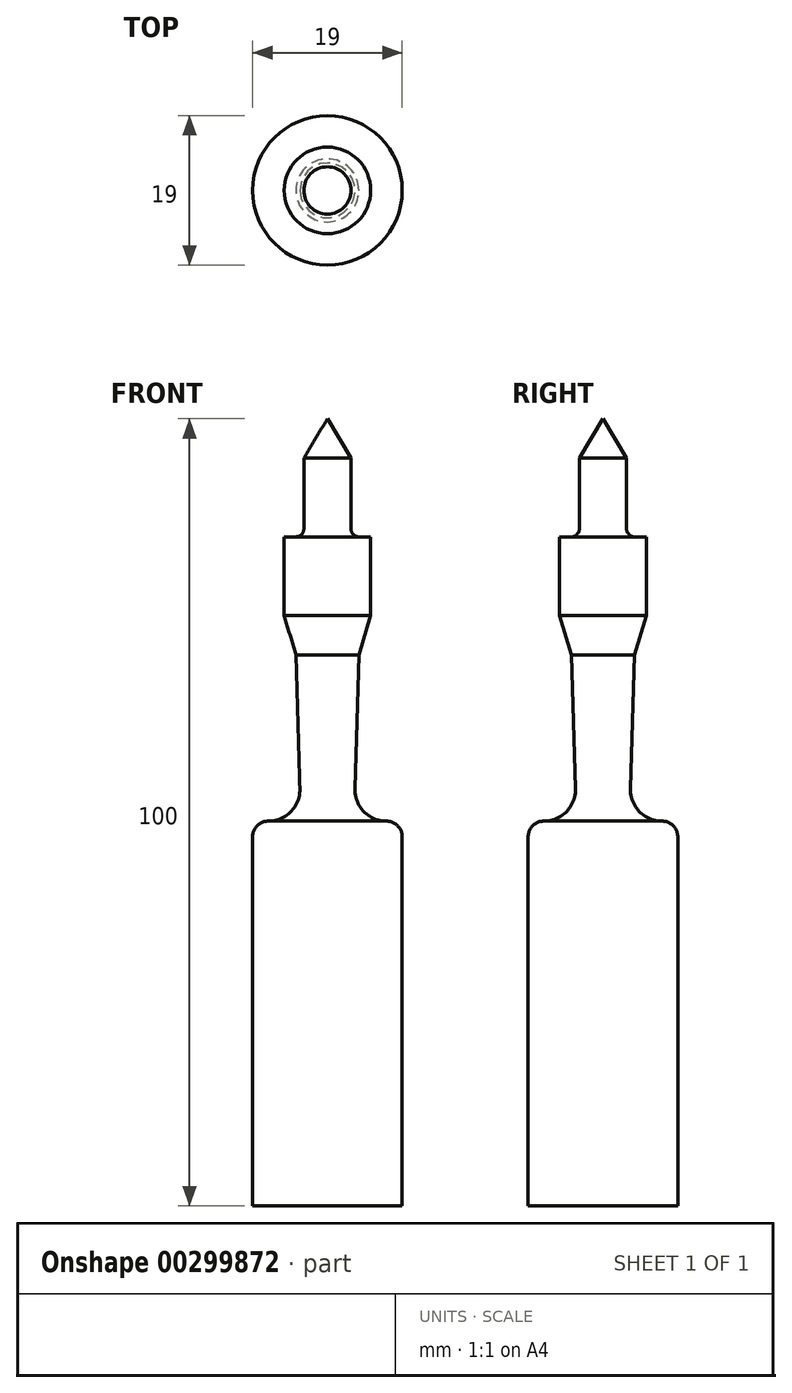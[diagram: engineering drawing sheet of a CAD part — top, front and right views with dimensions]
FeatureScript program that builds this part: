
annotation { "Feature Type Name" : "Feature", "Feature Type Description" : "" }
export const myFeature = defineFeature(function(context is Context, id is Id, definition is map)
    precondition{}
    {
        {
            var Q0;
            Q0=qCreatedBy(makeId("Front.planeOp"),FACE);
            var sketch = newSketch(context, id + "F0", { "sketchPlane" : qUnion([Q0])});
            skLineSegment(sketch, "E0", {"start": v(0, 0) * mm, "end": v(3, -5) * mm});
            skLineSegment(sketch, "E1", {"start": v(3, -5) * mm, "end": v(3, -14) * mm});
            skLineSegment(sketch, "E2", {"start": v(0, 0) * mm, "end": v(0, -100) * mm});
            skArc(sketch, "E3", {"start": v(3, -14) * mm, "mid": v(3.3, -14.7) * mm, "end": v(4, -15) * mm});
            skLineSegment(sketch, "E4", {"start": v(4, -15) * mm, "end": v(5.5, -15) * mm});
            skLineSegment(sketch, "E5", {"start": v(5.5, -15) * mm, "end": v(5.5, -25) * mm});
            skLineSegment(sketch, "E6", {"start": v(5.5, -25) * mm, "end": v(4, -30) * mm});
            skLineSegment(sketch, "E7", {"start": v(9.5, -53.12) * mm, "end": v(9.5, -100) * mm});
            skLineSegment(sketch, "E8", {"start": v(0, -100) * mm, "end": v(9.5, -100) * mm});
            skLineSegment(sketch, "E9", {"start": v(0, -100) * mm, "end": v(0, 0) * mm});
            skLineSegment(sketch, "E10", {"start": v(4, -30) * mm, "end": v(3.5, -47) * mm});
            skArc(sketch, "E11", {"start": v(3.5, -47) * mm, "mid": v(4.63, -49.9) * mm, "end": v(7.5, -51.12) * mm});
            skArc(sketch, "E12", {"start": v(9.5, -53.12) * mm, "mid": v(8.91, -51.7) * mm, "end": v(7.5, -51.12) * mm});
            skSolve(sketch);
        }
        {
            var Q0;
            Q0 = qSketchRegion(id + "F0", true);
            var Q1;
            Q1=sQuery(id+"F0.wireOp",EDGE,"E9");
            revolve(context, id + "F1", {"entities" : qUnion([Q0]), "axis" : qUnion([Q1]), "revolveType" : RevolveType.FULL});
        }
    });
